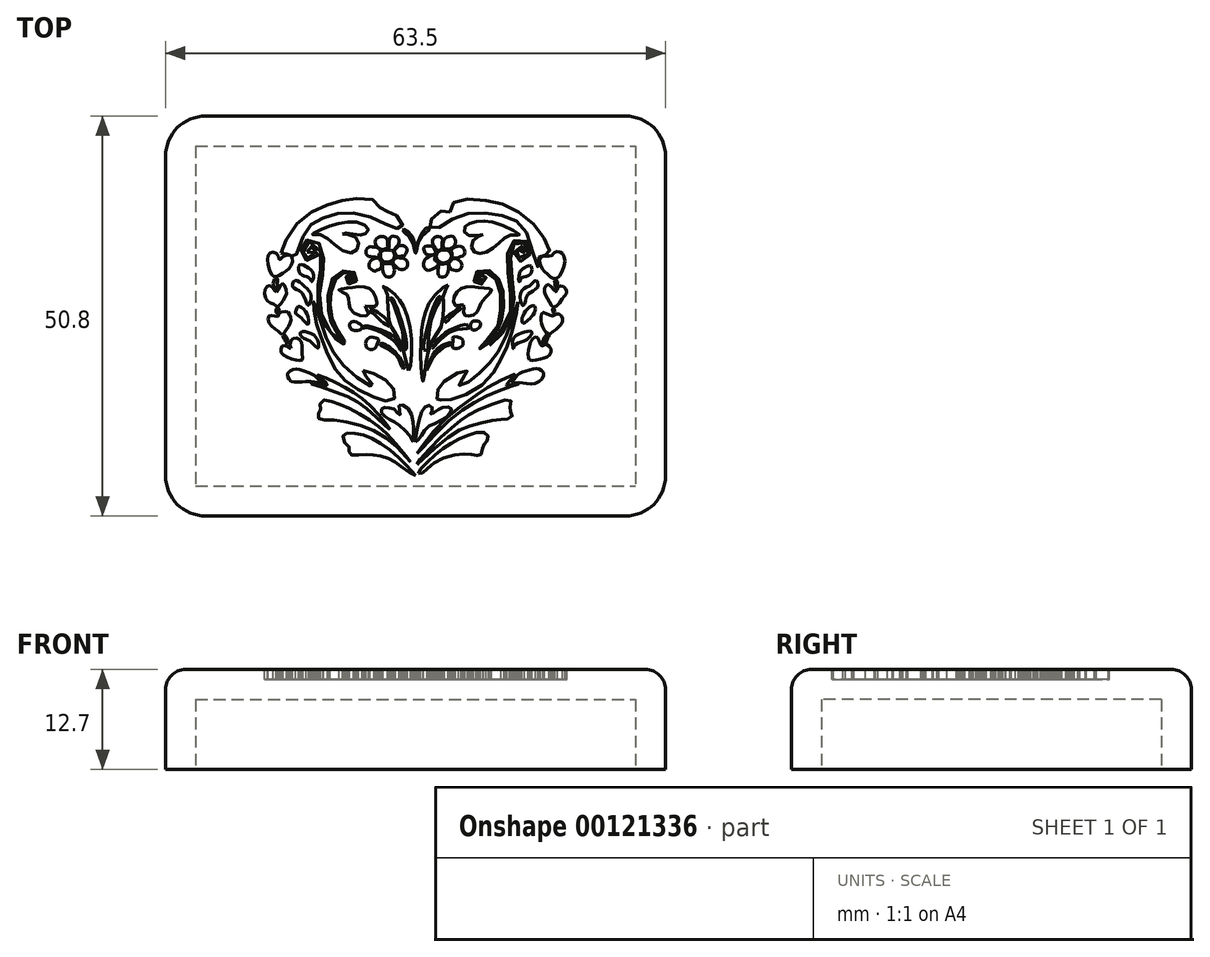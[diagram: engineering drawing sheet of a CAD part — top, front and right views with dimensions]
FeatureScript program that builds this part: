
annotation { "Feature Type Name" : "Feature", "Feature Type Description" : "" }
export const myFeature = defineFeature(function(context is Context, id is Id, definition is map)
    precondition{}
    {
        {
            var Q0;
            Q0=qCreatedBy(makeId("Top.planeOp"),FACE);
            var sketch = newSketch(context, id + "F0", { "sketchPlane" : qUnion([Q0])});
            skLineSegment(sketch, "E0.bottom", {"start": v(-31.75, 25.4) * mm, "end": v(31.75, 25.4) * mm});
            skLineSegment(sketch, "E0.top", {"start": v(-31.75, -25.4) * mm, "end": v(31.75, -25.4) * mm});
            skLineSegment(sketch, "E0.left", {"start": v(-31.75, 25.4) * mm, "end": v(-31.75, -25.4) * mm});
            skLineSegment(sketch, "E0.right", {"start": v(31.75, 25.4) * mm, "end": v(31.75, -25.4) * mm});
            skPoint(sketch, "E0.middle", {"position": v(0, 0) * mm});
            skSolve(sketch);
        }
        {
            var Q0;
            Q0=makeQuery(id+"F0.imprint","IMPRINT",FACE,{"disambiguationData":[TD([[makeQuery(id+"F0.imprint","IMPRINT",EDGE,{"derivedFrom":sQuery(id+"F0.wireOp",EDGE,"E0.bottom")}),-1.0]])]});
            extrude(context, id + "F1", {"entities" : qUnion([Q0]), "depth" : 12.7 * mm});
        }
        {
            var Q0;
            Q0=makeQuery(id+"F1.opExtrude","CAP_FACE",FACE,{"disambiguationData":[OSD([sQuery(id+"F0.wireOp",EDGE,"E0.bottom"),sQuery(id+"F0.wireOp",EDGE,"E0.top"),sQuery(id+"F0.wireOp",EDGE,"E0.left"),sQuery(id+"F0.wireOp",EDGE,"E0.right")])],"isStart":true});
            shell(context, id + "F2", {"entities" : qUnion([Q0]), "thickness" : 3.8 * mm});
        }
        {
            var Q0;
            Q0=makeQuery(id+"F1.opExtrude","CAP_EDGE",EDGE,{"disambiguationData":[OSD([sQuery(id+"F0.wireOp",EDGE,"E0.left")])],"isStart":false});
            var Q1;
            Q1=makeQuery(id+"F1.opExtrude","CAP_EDGE",EDGE,{"disambiguationData":[OSD([sQuery(id+"F0.wireOp",EDGE,"E0.bottom")])],"isStart":false});
            var Q2;
            Q2=makeQuery(id+"F1.opExtrude","CAP_EDGE",EDGE,{"disambiguationData":[OSD([sQuery(id+"F0.wireOp",EDGE,"E0.right")])],"isStart":false});
            var Q3;
            Q3=makeQuery(id+"F1.opExtrude","CAP_EDGE",EDGE,{"disambiguationData":[OSD([sQuery(id+"F0.wireOp",EDGE,"E0.top")])],"isStart":false});
            fillet(context, id + "F3", {"entities" : qUnion([Q0, Q1, Q2, Q3]), "radius" : 2.54 * mm, "tangentPropagation" : true, "allowEdgeOverflow" : false});
        }
        {
            var Q0;
            Q0=makeQuery(id+"F1.opExtrude","SWEPT_EDGE",EDGE,{"disambiguationData":[OSD([sQuery(id+"F0.wireOp",EDGE,"E0.top"),sQuery(id+"F0.wireOp",EDGE,"E0.left")])]});
            var Q1;
            Q1=makeQuery(id+"F1.opExtrude","SWEPT_EDGE",EDGE,{"disambiguationData":[OSD([sQuery(id+"F0.wireOp",EDGE,"E0.bottom"),sQuery(id+"F0.wireOp",EDGE,"E0.left")])]});
            var Q2;
            Q2=makeQuery(id+"F1.opExtrude","SWEPT_EDGE",EDGE,{"disambiguationData":[OSD([sQuery(id+"F0.wireOp",EDGE,"E0.top"),sQuery(id+"F0.wireOp",EDGE,"E0.right")])]});
            var Q3;
            Q3=makeQuery(id+"F1.opExtrude","SWEPT_EDGE",EDGE,{"disambiguationData":[OSD([sQuery(id+"F0.wireOp",EDGE,"E0.bottom"),sQuery(id+"F0.wireOp",EDGE,"E0.right")])]});
            fillet(context, id + "F4", {"entities" : qUnion([Q0, Q1, Q2, Q3]), "radius" : 5.08 * mm, "tangentPropagation" : true, "allowEdgeOverflow" : false});
        }
        {
            var Q0;
            Q0=makeQuery(id+"F1.opExtrude","CAP_FACE",FACE,{"disambiguationData":[OSD([sQuery(id+"F0.wireOp",EDGE,"E0.bottom"),sQuery(id+"F0.wireOp",EDGE,"E0.top"),sQuery(id+"F0.wireOp",EDGE,"E0.left"),sQuery(id+"F0.wireOp",EDGE,"E0.right")])],"isStart":false});
            var sketch = newSketch(context, id + "F5", { "sketchPlane" : qUnion([Q0])});
            skFitSpline(sketch, "E1", {"points": [v(0, -20.28) * mm, v(-0.7, -19.5) * mm, v(-2.26, -17.87) * mm, v(-4.82, -15.94) * mm, v(-6.68, -15.12) * mm, v(-8.41, -14.87) * mm, v(-9.2, -15.14) * mm, v(-8.99, -16.16) * mm, v(-8.37, -16.75) * mm, v(-8.44, -17.32) * mm, v(-8.05, -17.7) * mm, v(-6.68, -17.61) * mm, v(-5.52, -17.63) * mm, v(-4.08, -17.87) * mm, v(-2.7, -18.5) * mm, v(-1.52, -19.35) * mm, v(0, -20.28) * mm]});
            skFitSpline(sketch, "E2", {"points": [v(0.36, -20) * mm, v(1.37, -18.65) * mm, v(4, -16.5) * mm, v(6.38, -15.25) * mm, v(8.73, -14.8) * mm, v(9.26, -15.5) * mm, v(8.8, -16.18) * mm, v(8.54, -16.64) * mm, v(8.24, -17.66) * mm, v(7.57, -17.68) * mm, v(6.04, -17.53) * mm, v(2.47, -18.56) * mm, v(0.93, -19.88) * mm, v(0.36, -20) * mm]});
            skFitSpline(sketch, "E3", {"points": [v(0.17, -18.84) * mm, v(2.03, -16.62) * mm, v(5.8, -13.22) * mm, v(8.16, -11.86) * mm, v(12.07, -10.66) * mm, v(11.98, -11.53) * mm, v(12, -12.1) * mm, v(12.28, -12.67) * mm, v(11.77, -13.05) * mm, v(10.5, -13.17) * mm, v(7.46, -13.79) * mm, v(3.78, -15.65) * mm, v(0.17, -18.84) * mm]});
            skFitSpline(sketch, "E4", {"points": [v(-0.64, -18.56) * mm, v(-2.26, -16.73) * mm, v(-6.47, -14.08) * mm, v(-10.68, -13.22) * mm, v(-12.18, -13.11) * mm, v(-12.43, -12.58) * mm, v(-12.05, -12) * mm, v(-12.18, -11.46) * mm, v(-11.75, -10.7) * mm, v(-10.38, -10.95) * mm, v(-8.16, -11.88) * mm, v(-5.3, -13.58) * mm, v(-2.94, -15.7) * mm, v(-0.64, -18.56) * mm]});
            skFitSpline(sketch, "E5", {"points": [v(0.21, -17.47) * mm, v(3.38, -13.5) * mm, v(6.68, -10.83) * mm, v(9.51, -8.86) * mm, v(12.83, -7.36) * mm, v(12.34, -7.89) * mm, v(11.48, -8.71) * mm, v(12.07, -8.78) * mm, v(13.08, -8.63) * mm, v(11.46, -9.18) * mm, v(8.05, -10.68) * mm, v(3.49, -14) * mm, v(0.21, -17.47) * mm]});
            skFitSpline(sketch, "E6", {"points": [v(13.23, -7.3) * mm, v(14.52, -6.81) * mm, v(15.73, -6.73) * mm, v(16.3, -7.45) * mm, v(15.11, -8.6) * mm, v(13.21, -8.46) * mm, v(12.32, -8.46) * mm, v(12.68, -7.89) * mm, v(13.23, -7.3) * mm]});
            skFitSpline(sketch, "E7", {"points": [v(0, -16) * mm, v(0.3, -13.96) * mm, v(1.25, -11.5) * mm, v(1.96, -11.44) * mm, v(2.13, -11.88) * mm, v(1.92, -12.43) * mm, v(2.58, -12.1) * mm, v(3.47, -11.63) * mm, v(4.5, -11.7) * mm, v(4.29, -12.47) * mm, v(2.92, -13.43) * mm, v(1.37, -14.27) * mm, v(0.46, -15.6) * mm, v(0, -16) * mm]});
            skFitSpline(sketch, "E8", {"points": [v(-0.25, -15.05) * mm, v(-0.33, -13.5) * mm, v(-0.96, -11.71) * mm, v(-2.02, -11.3) * mm, v(-2.04, -11.93) * mm, v(-2.02, -12.6) * mm, v(-2.55, -11.99) * mm, v(-3.34, -11.67) * mm, v(-4.13, -11.64) * mm, v(-4.35, -12.02) * mm, v(-4.03, -12.68) * mm, v(-3.04, -13.27) * mm, v(-1.86, -14.03) * mm, v(-0.5, -15.6) * mm, v(-0.37, -16) * mm, v(-0.25, -15.05) * mm]});
            skFitSpline(sketch, "E9", {"points": [v(-3.23, -14.4) * mm, v(-5.72, -12.17) * mm, v(-9.47, -9.9) * mm, v(-13.38, -8.52) * mm, v(-12.53, -8.61) * mm, v(-11.13, -8.7) * mm, v(-12.6, -7.52) * mm, v(-11.37, -7.9) * mm, v(-8.16, -9.52) * mm, v(-5.3, -11.88) * mm, v(-3.23, -14.4) * mm]});
            skFitSpline(sketch, "E10", {"points": [v(-12.18, -8.16) * mm, v(-12.8, -7.6) * mm, v(-14.72, -6.79) * mm, v(-15.39, -6.76) * mm, v(-16.17, -7.16) * mm, v(-16.23, -7.74) * mm, v(-15.81, -8.28) * mm, v(-14.98, -8.41) * mm, v(-13.99, -8.32) * mm, v(-13.42, -8.34) * mm, v(-12.6, -8.41) * mm, v(-11.72, -8.52) * mm, v(-12.18, -8.16) * mm]});
            skFitSpline(sketch, "E11", {"points": [v(-6.65, -6.94) * mm, v(-6.42, -7.47) * mm, v(-6.04, -8.04) * mm, v(-5.27, -8.95) * mm, v(-6.73, -8.31) * mm, v(-9.8, -5.48) * mm, v(-11.64, -1.95) * mm, v(-13, 1.83) * mm, v(-12.78, 0) * mm, v(-12.12, -2.37) * mm, v(-10.43, -6.35) * mm, v(-8.55, -8.52) * mm, v(-5.23, -10.36) * mm, v(-3.41, -10.77) * mm, v(-2.55, -10.24) * mm, v(-3.18, -8.67) * mm, v(-4.92, -7.49) * mm, v(-6.65, -6.94) * mm]});
            skFitSpline(sketch, "E12", {"points": [v(13.03, 1.75) * mm, v(12.31, -1.74) * mm, v(11.02, -5.12) * mm, v(8.76, -8.48) * mm, v(4.5, -10.58) * mm, v(3.14, -10.66) * mm, v(2.8, -10.68) * mm, v(2.78, -9.54) * mm, v(3.7, -8.2) * mm, v(6.5, -6.94) * mm, v(6.35, -7.53) * mm, v(5.49, -8.76) * mm, v(6.71, -8.38) * mm, v(9.12, -6.24) * mm, v(11.21, -3.2) * mm, v(13.03, 1.75) * mm]});
            skFitSpline(sketch, "E13", {"points": [v(14.5, -5.59) * mm, v(14.34, -4.5) * mm, v(14.8, -2.94) * mm, v(15.48, -2.75) * mm, v(16.01, -3.79) * mm, v(16.41, -3.64) * mm, v(17.18, -4.09) * mm, v(16.94, -5.04) * mm, v(15.8, -5.48) * mm, v(14.5, -5.59) * mm]});
            skFitSpline(sketch, "E14", {"points": [v(16.86, -2.29) * mm, v(16.14, -1.42) * mm, v(15.9, -0.4) * mm, v(16.2, 0.46) * mm, v(17.3, 0) * mm, v(17.85, 0.27) * mm, v(18.55, 0) * mm, v(18.55, -0.96) * mm, v(17.64, -1.84) * mm, v(16.86, -2.29) * mm]});
            skFitSpline(sketch, "E15", {"points": [v(14.45, -1.93) * mm, v(13.4, -2.18) * mm, v(12.42, -2.86) * mm, v(12.33, -3.62) * mm, v(12.4, -4.15) * mm, v(12.7, -3.62) * mm, v(14.09, -3.03) * mm, v(14.79, -2.06) * mm, v(14.45, -1.93) * mm]});
            skFitSpline(sketch, "E16", {"points": [v(13.62, -0.9) * mm, v(13.73, 0.23) * mm, v(14.98, 1.33) * mm, v(15.2, 0.71) * mm, v(14.2, -0.64) * mm, v(13.62, -0.9) * mm]});
            skFitSpline(sketch, "E17", {"points": [v(17.53, 1.16) * mm, v(16.8, 2.13) * mm, v(16.37, 3.31) * mm, v(16.88, 4.01) * mm, v(17.79, 3.08) * mm, v(18.1, 3.67) * mm, v(18.8, 3.71) * mm, v(19.2, 3.1) * mm, v(18.68, 2.2) * mm, v(17.53, 1.16) * mm]});
            skFitSpline(sketch, "E18", {"points": [v(17.9, 4.75) * mm, v(16.8, 5.28) * mm, v(15.8, 6.59) * mm, v(16.03, 7.52) * mm, v(17.28, 7.65) * mm, v(17.58, 7.98) * mm, v(18.25, 8.18) * mm, v(18.95, 7.2) * mm, v(17.9, 4.75) * mm]});
            skFitSpline(sketch, "E19", {"points": [v(15.36, 4.54) * mm, v(14.55, 3.9) * mm, v(13.64, 3.4) * mm, v(13.29, 2.15) * mm, v(13.67, 1.33) * mm, v(14.03, 2.1) * mm, v(14.24, 2.7) * mm, v(15.1, 3.3) * mm, v(15.55, 3.88) * mm, v(15.36, 4.54) * mm]});
            skFitSpline(sketch, "E20", {"points": [v(-4.8, -3.45) * mm, v(-4.75, -2.97) * mm, v(-6, -2.8) * mm, v(-6.2, -3.96) * mm, v(-5.32, -4.2) * mm, v(-4.8, -3.45) * mm]});
            skFitSpline(sketch, "E21", {"points": [v(4.75, -3.24) * mm, v(4.75, -2.71) * mm, v(5.34, -2.67) * mm, v(5.95, -2.99) * mm, v(6.03, -3.58) * mm, v(5.55, -4.04) * mm, v(4.72, -3.98) * mm, v(4.75, -3.24) * mm]});
            skFitSpline(sketch, "E22", {"points": [v(-15.82, -4.1) * mm, v(-16.77, -3.73) * mm, v(-17.07, -4.6) * mm, v(-15.65, -5.46) * mm, v(-14.43, -5.59) * mm, v(-14.45, -4.68) * mm, v(-14.53, -3.18) * mm, v(-15.53, -2.86) * mm, v(-15.9, -3.68) * mm, v(-15.82, -4.1) * mm]});
            skFitSpline(sketch, "E23", {"points": [v(-16.94, -2.35) * mm, v(-16.37, -1.65) * mm, v(-15.82, -0.58) * mm, v(-16.01, 0.2) * mm, v(-16.48, 0.59) * mm, v(-17.43, 0.23) * mm, v(-17.43, 0) * mm, v(-17.83, 0) * mm, v(-18.61, 0) * mm, v(-18.55, -1.02) * mm, v(-17.32, -2.01) * mm, v(-16.94, -2.35) * mm]});
            skFitSpline(sketch, "E24", {"points": [v(-14.91, 1.22) * mm, v(-15.19, 0.71) * mm, v(-15.23, 0.37) * mm, v(-14.28, -0.5) * mm, v(-13.69, -1.06) * mm, v(-13.81, 0.31) * mm, v(-14.91, 1.22) * mm]});
            skFitSpline(sketch, "E25", {"points": [v(-14.6, -2.08) * mm, v(-14.34, -2.77) * mm, v(-13.5, -3.13) * mm, v(-12.4, -4.09) * mm, v(-12.33, -3.47) * mm, v(-13.01, -2.37) * mm, v(-14.6, -2.08) * mm]});
            skFitSpline(sketch, "E26", {"points": [v(-17.64, 3.06) * mm, v(-18.36, 3.78) * mm, v(-19.06, 3.5) * mm, v(-18.85, 1.92) * mm, v(-17.92, 1.47) * mm, v(-17.56, 1.18) * mm, v(-16.99, 1.75) * mm, v(-16.4, 3.14) * mm, v(-16.94, 4.1) * mm, v(-17.64, 3.06) * mm]});
            skFitSpline(sketch, "E27", {"points": [v(-17.7, 5) * mm, v(-16.6, 5.6) * mm, v(-15.76, 6.48) * mm, v(-15.82, 7.65) * mm, v(-16.71, 7.6) * mm, v(-17.28, 7.16) * mm, v(-17.51, 7.8) * mm, v(-18.4, 8.07) * mm, v(-18.8, 7.08) * mm, v(-18.15, 5.13) * mm, v(-17.7, 5) * mm]});
            skFitSpline(sketch, "E28", {"points": [v(-15.32, 4.5) * mm, v(-15.63, 3.76) * mm, v(-14.47, 2.95) * mm, v(-13.65, 1.37) * mm, v(-13.24, 2.5) * mm, v(-14.11, 3.8) * mm, v(-15.32, 4.5) * mm]});
            skFitSpline(sketch, "E29", {"points": [v(-14.7, 6.46) * mm, v(-14.68, 5.38) * mm, v(-13.52, 4.86) * mm, v(-13.18, 4.37) * mm, v(-12.95, 5.15) * mm, v(-13.54, 6.04) * mm, v(-14.7, 6.46) * mm]});
            skFitSpline(sketch, "E30", {"points": [v(-3.1, 6.98) * mm, v(-3.96, 6.9) * mm, v(-4.38, 7.28) * mm, v(-4.37, 8.14) * mm, v(-3.6, 8.38) * mm, v(-2.86, 8.2) * mm, v(-2.69, 7.56) * mm, v(-3.1, 6.98) * mm]});
            skFitSpline(sketch, "E31", {"points": [v(2.63, 7.6) * mm, v(2.88, 8.15) * mm, v(3.45, 8.4) * mm, v(4.3, 8.2) * mm, v(4.52, 7.43) * mm, v(4.07, 6.9) * mm, v(3.17, 6.83) * mm, v(2.63, 7.6) * mm]});
            skFitSpline(sketch, "E32", {"points": [v(-6.4, 1.27) * mm, v(-5.98, 0.48) * mm, v(-6.3, 0) * mm, v(-8.1, 0.64) * mm, v(-8.45, 1.93) * mm, v(-8.83, 2.79) * mm, v(-9.72, 3.33) * mm, v(-9.02, 3.49) * mm, v(-7.44, 3.7) * mm, v(-5.82, 3.49) * mm, v(-5.06, 2.31) * mm, v(-5.06, 1.2) * mm, v(-6.4, 1.27) * mm]});
            skFitSpline(sketch, "E33", {"points": [v(-7.95, -0.7) * mm, v(-8.4, -1.23) * mm, v(-7.7, -1.87) * mm, v(-6.77, -1.42) * mm, v(-7.95, -0.7) * mm]});
            skFitSpline(sketch, "E34", {"points": [v(7.13, -0.82) * mm, v(7, -1.42) * mm, v(7.48, -1.8) * mm, v(8.27, -1.14) * mm, v(7.83, -0.63) * mm, v(7.13, -0.82) * mm]});
            skFitSpline(sketch, "E35", {"points": [v(6.08, 1.43) * mm, v(6.08, 0.54) * mm, v(6.5, 0) * mm, v(7.73, 0.45) * mm, v(8.4, 1.8) * mm, v(9.66, 3.3) * mm, v(8.68, 3.55) * mm, v(6.37, 3.68) * mm, v(4.98, 2.63) * mm, v(5.07, 1.33) * mm, v(6.08, 1.43) * mm]});
            skFitSpline(sketch, "E36", {"points": [v(-9.28, 10.4) * mm, v(-8.02, 10.22) * mm, v(-7.21, 9.1) * mm, v(-7.95, 8.06) * mm, v(-10.1, 8.9) * mm, v(-12.05, 10.31) * mm, v(-13.2, 10.34) * mm, v(-12.08, 10.96) * mm, v(-9.54, 11.8) * mm, v(-7.2, 11.83) * mm, v(-6, 11) * mm, v(-6.36, 10.46) * mm, v(-7.43, 10.31) * mm, v(-8.97, 10.55) * mm, v(-9.28, 10.4) * mm]});
            skFitSpline(sketch, "E37", {"points": [v(-17.06, 7.98) * mm, v(-15.82, 10.74) * mm, v(-12.85, 13.45) * mm, v(-9.83, 14.53) * mm, v(-7.28, 14.94) * mm, v(-4.87, 14.47) * mm, v(-4.29, 13.35) * mm, v(-2.99, 13.25) * mm, v(-2.1, 12.31) * mm, v(-1.63, 11.34) * mm, v(-2.41, 11.12) * mm, v(-4.17, 11.9) * mm, v(-7.4, 13) * mm, v(-10.41, 12.91) * mm, v(-12.79, 11.93) * mm, v(-14.16, 10.36) * mm, v(-15.4, 7.43) * mm, v(-15.65, 7.56) * mm, v(-15.82, 7.8) * mm, v(-16.25, 7.85) * mm, v(-16.83, 7.8) * mm, v(-17.06, 7.98) * mm]});
            skFitSpline(sketch, "E38", {"points": [v(-1.67, 10.9) * mm, v(-0.56, 9.75) * mm, v(0, 8) * mm, v(0.22, 8.86) * mm, v(0.79, 10.14) * mm, v(1.75, 11) * mm, v(1.6, 11.23) * mm, v(0.86, 10.6) * mm, v(0, 8.9) * mm, v(-0.2, 9.49) * mm, v(-0.44, 10.14) * mm, v(-1.38, 11) * mm, v(-1.67, 10.9) * mm]});
            skFitSpline(sketch, "E39", {"points": [v(4.41, 13.24) * mm, v(3.36, 13.36) * mm, v(1.92, 12.19) * mm, v(1.8, 11.37) * mm, v(2.56, 11.1) * mm, v(5.23, 12.6) * mm, v(8.64, 13.11) * mm, v(12.22, 12.4) * mm, v(14.24, 10.23) * mm, v(15.53, 6.25) * mm, v(15.68, 7.39) * mm, v(16, 7.77) * mm, v(16.95, 7.8) * mm, v(16.92, 8.71) * mm, v(15.22, 11.43) * mm, v(11.58, 14) * mm, v(7.94, 14.8) * mm, v(4.84, 14.4) * mm, v(4.41, 13.24) * mm]});
            skFitSpline(sketch, "E40", {"points": [v(8.54, 10.36) * mm, v(6.67, 10.25) * mm, v(6.2, 11.23) * mm, v(7.54, 11.96) * mm, v(10.3, 11.78) * mm, v(13.23, 10.29) * mm, v(12.16, 10.29) * mm, v(10.55, 9.19) * mm, v(8.57, 8.01) * mm, v(7.33, 8.26) * mm, v(7.38, 9.68) * mm, v(8.54, 10.36) * mm]});
            skFitSpline(sketch, "E41", {"points": [v(2.46, 7.66) * mm, v(1.52, 7.46) * mm, v(0.98, 6.6) * mm, v(1.2, 6) * mm, v(1.9, 5.84) * mm, v(2.95, 6.72) * mm, v(2.44, 7.13) * mm, v(2.46, 7.66) * mm]});
            skFitSpline(sketch, "E42", {"points": [v(3.03, 6.56) * mm, v(2.86, 5.79) * mm, v(3.05, 5.05) * mm, v(3.78, 5.05) * mm, v(4.16, 5.85) * mm, v(4.1, 6.63) * mm, v(3.46, 6.58) * mm, v(3.03, 6.56) * mm]});
            skFitSpline(sketch, "E43", {"points": [v(4.26, 6.79) * mm, v(4.31, 6.3) * mm, v(4.68, 5.88) * mm, v(5.52, 5.84) * mm, v(5.89, 6.43) * mm, v(5.33, 7.21) * mm, v(4.74, 7.27) * mm, v(4.51, 7.02) * mm, v(4.26, 6.79) * mm]});
            skFitSpline(sketch, "E44", {"points": [v(4.52, 8.28) * mm, v(4.98, 8.77) * mm, v(5.9, 8.77) * mm, v(6.26, 8.25) * mm, v(6.15, 7.77) * mm, v(5.47, 7.45) * mm, v(4.7, 7.43) * mm, v(4.64, 7.83) * mm, v(4.52, 8.28) * mm]});
            skFitSpline(sketch, "E45", {"points": [v(3.54, 8.7) * mm, v(3.57, 9.6) * mm, v(4.01, 10.03) * mm, v(4.74, 10.12) * mm, v(5.04, 9.65) * mm, v(5, 9.02) * mm, v(4.44, 8.57) * mm, v(4.23, 8.5) * mm, v(3.9, 8.5) * mm, v(3.54, 8.7) * mm]});
            skFitSpline(sketch, "E46", {"points": [v(2.8, 8.3) * mm, v(2.49, 8.7) * mm, v(2.13, 9.4) * mm, v(2.44, 10.02) * mm, v(3.15, 10.04) * mm, v(3.4, 9.65) * mm, v(3.36, 9.25) * mm, v(3.37, 8.85) * mm, v(3.35, 8.57) * mm, v(3.03, 8.38) * mm, v(2.8, 8.3) * mm]});
            skFitSpline(sketch, "E47", {"points": [v(2.45, 7.9) * mm, v(1.57, 7.77) * mm, v(1.13, 8.15) * mm, v(1.08, 8.69) * mm, v(1.58, 8.89) * mm, v(2.2, 8.86) * mm, v(2.34, 8.56) * mm, v(2.53, 8.23) * mm, v(2.45, 7.9) * mm]});
            skFitSpline(sketch, "E48", {"points": [v(-0.87, -6.91) * mm, v(-0.5, -3.36) * mm, v(-1.5, 1.19) * mm, v(-2.88, 2.96) * mm, v(-4.1, 3.76) * mm, v(-3.62, 3.05) * mm, v(-3.56, 2.14) * mm, v(-3.43, 0.32) * mm, v(-3.26, -0.97) * mm, v(-2.54, -2.26) * mm, v(-1.49, -4.5) * mm, v(-0.87, -6.91) * mm]});
            skFitSpline(sketch, "E49", {"points": [v(-3.24, 2.2) * mm, v(-2.99, 1.82) * mm, v(-2.4, 0.36) * mm, v(-1.6, -2.6) * mm, v(-1.53, -3.94) * mm, v(-1.2, -4.26) * mm, v(-1.49, -1.73) * mm, v(-2.68, 1.78) * mm, v(-3.1, 2.34) * mm, v(-3.24, 2.2) * mm]});
            skFitSpline(sketch, "E50", {"points": [v(4.13, 3.93) * mm, v(2.58, 2.83) * mm, v(1.25, 0.44) * mm, v(0.73, -2.31) * mm, v(0.72, -6.65) * mm, v(0.91, -8.28) * mm, v(1.34, -5.94) * mm, v(2.26, -2.88) * mm, v(3.31, -1.12) * mm, v(3.53, 1.65) * mm, v(3.53, 1.95) * mm, v(3.58, 2.9) * mm, v(4.13, 3.93) * mm]});
            skFitSpline(sketch, "E51", {"points": [v(1.1, -4.34) * mm, v(1.46, -1.55) * mm, v(2.26, 1.07) * mm, v(3.06, 2.54) * mm, v(3.17, 2.35) * mm, v(2.73, 1.31) * mm, v(1.94, -0.8) * mm, v(1.6, -3.45) * mm, v(1.45, -4.36) * mm, v(1.1, -4.34) * mm]});
            skFitSpline(sketch, "E52", {"points": [v(6.64, -1.14) * mm, v(4.95, -1.51) * mm, v(2.65, -3.18) * mm, v(2.17, -4.09) * mm, v(2.78, -3.38) * mm, v(3.85, -2.44) * mm, v(5.12, -1.76) * mm, v(6.76, -1.53) * mm, v(6.7, -1.4) * mm, v(6.64, -1.14) * mm]});
            skFitSpline(sketch, "E53", {"points": [v(3.72, -0.8) * mm, v(5.1, 0.39) * mm, v(5.75, 0.98) * mm, v(5.4, 1.08) * mm, v(5.16, 0.76) * mm, v(3.83, -0.21) * mm, v(3.67, -0.59) * mm, v(3.72, -0.8) * mm]});
            skFitSpline(sketch, "E54", {"points": [v(1.43, -6.93) * mm, v(2.28, -5.2) * mm, v(4.02, -3.77) * mm, v(4.34, -3.64) * mm, v(4.54, -3.43) * mm, v(3.93, -3.49) * mm, v(2.33, -4.7) * mm, v(1.43, -6.93) * mm]});
            skFitSpline(sketch, "E55", {"points": [v(-1.58, -6.68) * mm, v(-2.44, -5) * mm, v(-4.5, -3.66) * mm, v(-4.48, -3.5) * mm, v(-3.88, -3.6) * mm, v(-2.97, -4.21) * mm, v(-1.88, -5.47) * mm, v(-1.41, -6.6) * mm, v(-1.58, -6.68) * mm]});
            skFitSpline(sketch, "E56", {"points": [v(-1.77, -4.45) * mm, v(-2.97, -2.97) * mm, v(-6.46, -1.5) * mm, v(-6.6, -1.58) * mm, v(-6.6, -1.4) * mm, v(-6.37, -1.24) * mm, v(-4.58, -1.72) * mm, v(-2.35, -3) * mm, v(-1.77, -4.45) * mm]});
            skFitSpline(sketch, "E57", {"points": [v(-5.75, 0.84) * mm, v(-3.41, -1.27) * mm, v(-3.44, -0.84) * mm, v(-4.86, 0.5) * mm, v(-5.75, 0.84) * mm]});
            skFitSpline(sketch, "E58", {"points": [v(-4.08, 6.62) * mm, v(-4.14, 5.75) * mm, v(-3.67, 4.97) * mm, v(-2.81, 5.27) * mm, v(-2.78, 6.4) * mm, v(-2.95, 6.63) * mm, v(-3.58, 6.67) * mm, v(-4.08, 6.62) * mm]});
            skFitSpline(sketch, "E59", {"points": [v(-5.2, 5.73) * mm, v(-5.82, 6.08) * mm, v(-5.88, 6.6) * mm, v(-5.52, 7.17) * mm, v(-4.62, 7.3) * mm, v(-4.41, 6.96) * mm, v(-4.26, 6.8) * mm, v(-4.32, 6.53) * mm, v(-4.38, 6.15) * mm, v(-4.92, 5.8) * mm, v(-5.2, 5.73) * mm]});
            skFitSpline(sketch, "E60", {"points": [v(-5.92, 8.76) * mm, v(-6.31, 8.14) * mm, v(-6.03, 7.61) * mm, v(-5.38, 7.51) * mm, v(-4.64, 7.48) * mm, v(-4.62, 7.8) * mm, v(-4.47, 8.24) * mm, v(-4.9, 8.7) * mm, v(-5.37, 8.77) * mm, v(-5.92, 8.76) * mm]});
            skFitSpline(sketch, "E61", {"points": [v(-5, 8.94) * mm, v(-5.1, 9.48) * mm, v(-4.79, 9.96) * mm, v(-4.23, 10.11) * mm, v(-3.63, 9.83) * mm, v(-3.55, 9.2) * mm, v(-3.55, 8.63) * mm, v(-3.9, 8.55) * mm, v(-4.3, 8.44) * mm, v(-4.54, 8.61) * mm, v(-5, 8.94) * mm]});
            skFitSpline(sketch, "E62", {"points": [v(-3.39, 8.5) * mm, v(-3.38, 8.88) * mm, v(-3.39, 9.5) * mm, v(-3.18, 10) * mm, v(-2.72, 10.15) * mm, v(-2.14, 9.79) * mm, v(-2.14, 9.23) * mm, v(-2.4, 8.81) * mm, v(-2.51, 8.71) * mm, v(-2.77, 8.36) * mm, v(-3.02, 8.3) * mm, v(-3.39, 8.5) * mm]});
            skFitSpline(sketch, "E63", {"points": [v(-2.66, 8.3) * mm, v(-2.2, 8.86) * mm, v(-1.78, 8.96) * mm, v(-1.2, 8.75) * mm, v(-1.1, 8.3) * mm, v(-1.37, 7.71) * mm, v(-1.9, 7.59) * mm, v(-2.4, 7.6) * mm, v(-2.52, 7.8) * mm, v(-2.62, 8.03) * mm, v(-2.66, 8.3) * mm]});
            skFitSpline(sketch, "E64", {"points": [v(-2.84, 7.01) * mm, v(-2.88, 6.78) * mm, v(-2.49, 6.28) * mm, v(-2.03, 5.96) * mm, v(-1.47, 5.93) * mm, v(-1.11, 6.16) * mm, v(-1.03, 6.67) * mm, v(-1.25, 7.16) * mm, v(-1.72, 7.35) * mm, v(-1.86, 7.37) * mm, v(-2.4, 7.4) * mm, v(-2.84, 7.01) * mm]});
            skFitSpline(sketch, "E65", {"points": [v(14.5, 6.4) * mm, v(14.06, 6.28) * mm, v(13.43, 5.84) * mm, v(13.13, 5.17) * mm, v(13.17, 4.33) * mm, v(13.38, 4.74) * mm, v(13.75, 4.95) * mm, v(14.65, 5.37) * mm, v(14.73, 6.25) * mm, v(14.5, 6.4) * mm]});
            skFitSpline(sketch, "E66", {"points": [v(-13.75, 8.15) * mm, v(-13.57, 8.35) * mm, v(-13.2, 8.5) * mm, v(-12.72, 7.97) * mm, v(-13, 7.49) * mm, v(-13.56, 7.39) * mm, v(-13.84, 7.39) * mm, v(-14.04, 7.6) * mm, v(-14.23, 7.68) * mm, v(-14.26, 8.3) * mm, v(-14.14, 8.95) * mm, v(-13.28, 9.52) * mm, v(-12.2, 8.67) * mm, v(-12.09, 7.39) * mm, v(-12.1, 5.78) * mm, v(-12.2, 4.99) * mm, v(-12.45, 3.34) * mm, v(-12.37, 1.24) * mm, v(-12.25, 0.52) * mm, v(-11.2, -1.8) * mm, v(-10.04, -2.97) * mm, v(-9.07, -3.79) * mm, v(-9.04, -3.6) * mm, v(-9.2, -3.46) * mm, v(-10.54, -2.34) * mm, v(-11.65, -0.54) * mm, v(-12.1, 1.04) * mm, v(-12.14, 3.2) * mm, v(-11.87, 4.93) * mm, v(-11.68, 6.04) * mm, v(-11.7, 7.47) * mm, v(-11.85, 8.5) * mm, v(-12.59, 9.58) * mm, v(-13.36, 9.75) * mm, v(-14.12, 9.45) * mm, v(-14.48, 8.98) * mm, v(-14.53, 8.1) * mm, v(-14.38, 7.46) * mm, v(-13.68, 7.02) * mm, v(-12.68, 7.2) * mm, v(-12.4, 7.97) * mm, v(-12.64, 8.69) * mm, v(-13.18, 8.83) * mm, v(-13.82, 8.54) * mm, v(-13.9, 8.13) * mm, v(-13.75, 8.15) * mm]});
            skFitSpline(sketch, "E67", {"points": [v(-9.5, -3.06) * mm, v(-10.82, -0.62) * mm, v(-10.84, -0.56) * mm, v(-11.15, 1.55) * mm, v(-11.1, 2.7) * mm, v(-10.4, 4.99) * mm, v(-9.43, 5.7) * mm, v(-8.38, 5.78) * mm, v(-7.6, 5.38) * mm, v(-7.46, 4.82) * mm, v(-7.75, 4.07) * mm, v(-8.4, 4.02) * mm, v(-8.78, 4.4) * mm, v(-8.84, 4.9) * mm, v(-8.64, 5.26) * mm, v(-8.12, 5.35) * mm, v(-7.92, 5.09) * mm, v(-7.88, 4.66) * mm, v(-8.07, 4.66) * mm, v(-8.13, 4.88) * mm, v(-8.3, 5.01) * mm, v(-8.44, 5) * mm, v(-8.72, 4.85) * mm, v(-8.6, 4.5) * mm, v(-8.56, 4.4) * mm, v(-8.13, 4.16) * mm, v(-7.8, 4.4) * mm, v(-7.67, 4.88) * mm, v(-7.79, 5.22) * mm, v(-7.94, 5.36) * mm, v(-8.49, 5.56) * mm, v(-9.43, 5.4) * mm, v(-10.11, 4.75) * mm, v(-10.64, 3.46) * mm, v(-10.88, 2.32) * mm, v(-10.83, 1.09) * mm, v(-10.54, -0.5) * mm, v(-9.97, -1.72) * mm, v(-9.27, -2.93) * mm, v(-8.94, -3.39) * mm, v(-9.12, -3.33) * mm, v(-9.5, -3.06) * mm]});
            skFitSpline(sketch, "E68", {"points": [v(8.06, 4.75) * mm, v(8.3, 4.96) * mm, v(8.64, 4.63) * mm, v(8.21, 4.22) * mm, v(7.8, 4.44) * mm, v(7.7, 4.99) * mm, v(7.92, 5.32) * mm, v(8.58, 5.53) * mm, v(9.47, 5.34) * mm, v(10.43, 4.28) * mm, v(10.85, 2.36) * mm, v(10.7, -0.14) * mm, v(9.9, -2.13) * mm, v(8.02, -4.14) * mm, v(8.16, -4.14) * mm, v(8.85, -3.7) * mm, v(9.76, -2.73) * mm, v(10.83, -0.96) * mm, v(10.94, -0.22) * mm, v(11.22, 1.68) * mm, v(11, 3.63) * mm, v(10.43, 4.9) * mm, v(9.38, 5.77) * mm, v(7.85, 5.68) * mm, v(7.39, 4.83) * mm, v(7.61, 4.12) * mm, v(8.3, 4.01) * mm, v(8.85, 4.34) * mm, v(8.93, 5) * mm, v(8.42, 5.3) * mm, v(7.95, 5.18) * mm, v(7.88, 4.75) * mm, v(8.06, 4.75) * mm]});
            skFitSpline(sketch, "E69", {"points": [v(9.38, -3.73) * mm, v(10.51, -2.72) * mm, v(11.6, -1.28) * mm, v(12.37, 0.72) * mm, v(12.48, 2.73) * mm, v(12.18, 5.28) * mm, v(12.1, 7.54) * mm, v(12.23, 8.77) * mm, v(12.77, 9.35) * mm, v(13.38, 9.46) * mm, v(14, 9.13) * mm, v(14.3, 8.32) * mm, v(14.17, 7.53) * mm, v(13.28, 7.29) * mm, v(12.78, 7.64) * mm, v(12.75, 8.13) * mm, v(13.12, 8.58) * mm, v(13.66, 8.38) * mm, v(13.72, 8.05) * mm, v(13.81, 8.07) * mm, v(13.86, 8.2) * mm, v(13.76, 8.67) * mm, v(13.26, 8.9) * mm, v(12.64, 8.55) * mm, v(12.52, 7.67) * mm, v(12.93, 7.05) * mm, v(13.8, 7) * mm, v(14.43, 7.55) * mm, v(14.55, 8.61) * mm, v(14.22, 9.42) * mm, v(13.38, 9.85) * mm, v(12.18, 9.32) * mm, v(11.67, 8.12) * mm, v(11.72, 6.39) * mm, v(11.92, 3.85) * mm, v(12.2, 1.62) * mm, v(11.82, -0.12) * mm, v(10.4, -2.4) * mm, v(9.38, -3.73) * mm]});
            skFitSpline(sketch, "E70", {"points": [v(-17.92, 4.7) * mm, v(-17.92, 3.5) * mm, v(-17.56, 3.53) * mm, v(-17.56, 4.05) * mm, v(-17.56, 4.3) * mm, v(-17.56, 4.72) * mm, v(-17.92, 4.7) * mm]});
            skFitSpline(sketch, "E71", {"points": [v(-17.65, 0.96) * mm, v(-17.66, 0.39) * mm, v(-17.57, 0.4) * mm, v(-17.4, 0.63) * mm, v(-17.4, 1) * mm, v(-17.65, 0.96) * mm]});
            skFitSpline(sketch, "E72", {"points": [v(-16.76, -2.78) * mm, v(-16.28, -3.57) * mm, v(-16.2, -3.4) * mm, v(-16.28, -2.97) * mm, v(-16.68, -2.41) * mm, v(-16.82, -2.58) * mm, v(-16.76, -2.78) * mm]});
            skFitSpline(sketch, "E73", {"points": [v(16.18, -3.25) * mm, v(16.66, -2.46) * mm, v(16.96, -2.46) * mm, v(16.75, -2.86) * mm, v(16.5, -3.48) * mm, v(16.18, -3.25) * mm]});
            skFitSpline(sketch, "E74", {"points": [v(17.48, 0.45) * mm, v(17.44, 0.96) * mm, v(17.56, 0.96) * mm, v(17.68, 0.45) * mm, v(17.6, 0.34) * mm, v(17.48, 0.45) * mm]});
            skFitSpline(sketch, "E75", {"points": [v(17.7, 3.76) * mm, v(17.7, 4.2) * mm, v(17.7, 4.5) * mm, v(17.93, 4.54) * mm, v(18.01, 4) * mm, v(17.9, 3.6) * mm, v(17.7, 3.76) * mm]});
            skSolve(sketch);
        }
        {
            var Q0;
            Q0=qSketchRegion(id+"F5",true);
            extrude(context, id + "F6", {"entities" : qUnion([Q0]), "operationType" : NewBodyOperationType.REMOVE, "oppositeDirection" : true, "depth" : 1.27 * mm});
        }
    });
